# Revit family: Fixture_Support-Wood-Stud_Water_Closet-Zurn-Z1282-HD4_Hub
name_source: partatom
category: Plumbing Fixtures
units: mm (PartAtom-declared; Revit-internal decimal feet)

## family parameters
Always vertical = Yes
Cut with Voids When Loaded = No
Maintain Annotation Orientation = No
OmniClass Number = 23.45.05.21.11
OmniClass Title = Water Closets
Part Type = Normal
Room Calculation Point = No
Round Connector Dimension = Use Radius
Shared = No
Work Plane-Based = No

## types (1)
- Z1282-HD 4 Inch Hub and Spigot Fitting
    Approx. Wt = 54
    Assembly Code = D2010110
    Bracket = Iron - Zurn -Cast - Painted - Blue
    CW Connection = No
    CWFU = 0
    Coupling = ABS - Zurn - Acrylonitrile Butadiene Styrene - Black
    Default Elevation = 0 "
    Description = WOOD STUD SUPPORTED HUB AND SPIGOT WATER CLOSET CARRIER
    Fitting = Iron - Zurn -Cast - Painted - Blue
    HW Connection = No
    HWFU = 0
    Hardware = Steel - Zurn - Stainless - Type - 304
    Height = 15.25 "
    Hub Vent Connection Radius = 2 "
    Manufacturer = Zurn Water, LLC
    Manufacturer Brand = Zurn
    Model = Z1282
    Modified Date = 11/26/2025
    Product Documentation Link = https://www.zurn.com
    Product Page URL = https://www.zurn.com
    Product data url = https://bimobject.com
    Sanitary Outlet Connection Radius = 2 "
    URL = www.zurn.com
    Vent Connection = Yes
    WFU = 1
    Waste Connection = Yes
    Water Closet Inlet Radius = 2 "

## geometry (parser evidence)
native form markers: Sweep x1
no freeform markers — native parametric forms only
